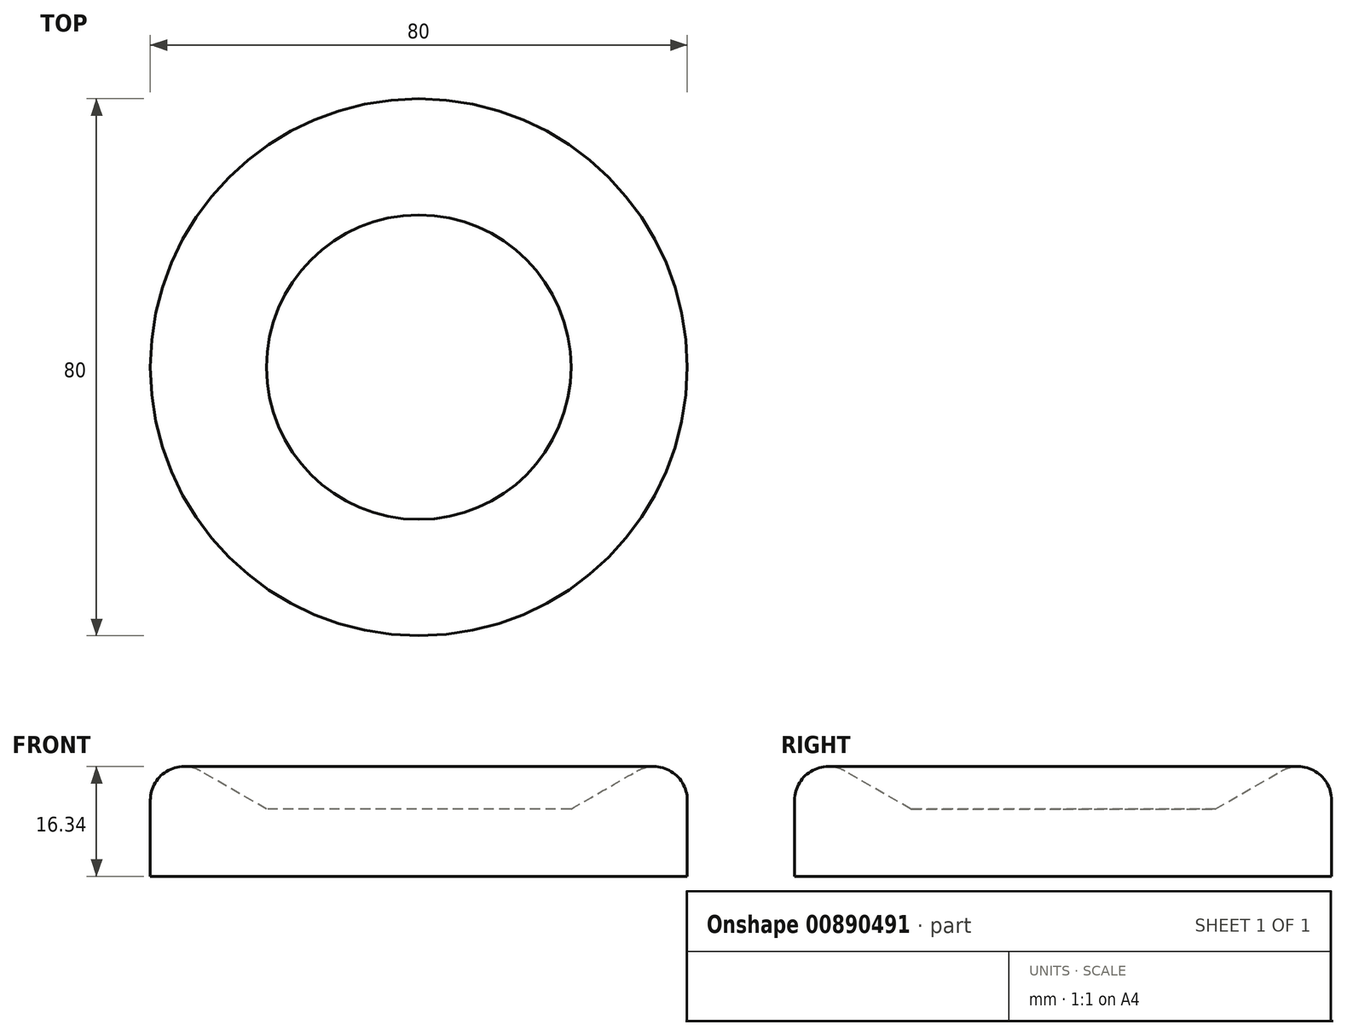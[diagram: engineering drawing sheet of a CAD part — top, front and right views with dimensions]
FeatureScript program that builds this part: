
annotation { "Feature Type Name" : "Feature", "Feature Type Description" : "" }
export const myFeature = defineFeature(function(context is Context, id is Id, definition is map)
    precondition{}
    {
        {
            var Q0;
            Q0=qCreatedBy(makeId("Front.planeOp"),FACE);
            var sketch = newSketch(context, id + "F0", { "sketchPlane" : qUnion([Q0])});
            skLineSegment(sketch, "E0", {"start": v(0, 0) * mm, "end": v(-40, 0) * mm});
            skLineSegment(sketch, "E1", {"start": v(-40, 0) * mm, "end": v(-40, 20) * mm});
            skLineSegment(sketch, "E2", {"start": v(-40, 20) * mm, "end": v(-22.68, 10) * mm});
            skLineSegment(sketch, "E3", {"start": v(-22.68, 10) * mm, "end": v(0, 10) * mm});
            skLineSegment(sketch, "E4", {"start": v(0, 10) * mm, "end": v(0, 0) * mm});
            skSolve(sketch);
        }
        {
            var Q0;
            Q0=makeQuery(id+"F0.imprint","IMPRINT",FACE,{"disambiguationData":[TD([[makeQuery(id+"F0.imprint","IMPRINT",EDGE,{"derivedFrom":sQuery(id+"F0.wireOp",EDGE,"E0")}),-1.0]])]});
            var Q1;
            Q1=sQuery(id+"F0.wireOp",EDGE,"E4");
            revolve(context, id + "F1", {"surfaceOperationType" : NewSurfaceOperationType.NEW, "entities" : qUnion([Q0]), "axis" : qUnion([Q1]), "revolveType" : RevolveType.FULL});
        }
        {
            var Q0;
            Q0=makeQuery(id+"F1.opRevolve","SWEPT_EDGE",EDGE,{"disambiguationData":[OSD([sQuery(id+"F0.wireOp",EDGE,"E1"),sQuery(id+"F0.wireOp",EDGE,"E2")])]});
            fillet(context, id + "F2", {"entities" : qUnion([Q0]), "radius" : 5 * mm, "tangentPropagation" : true, "allowEdgeOverflow" : false});
        }
    });
